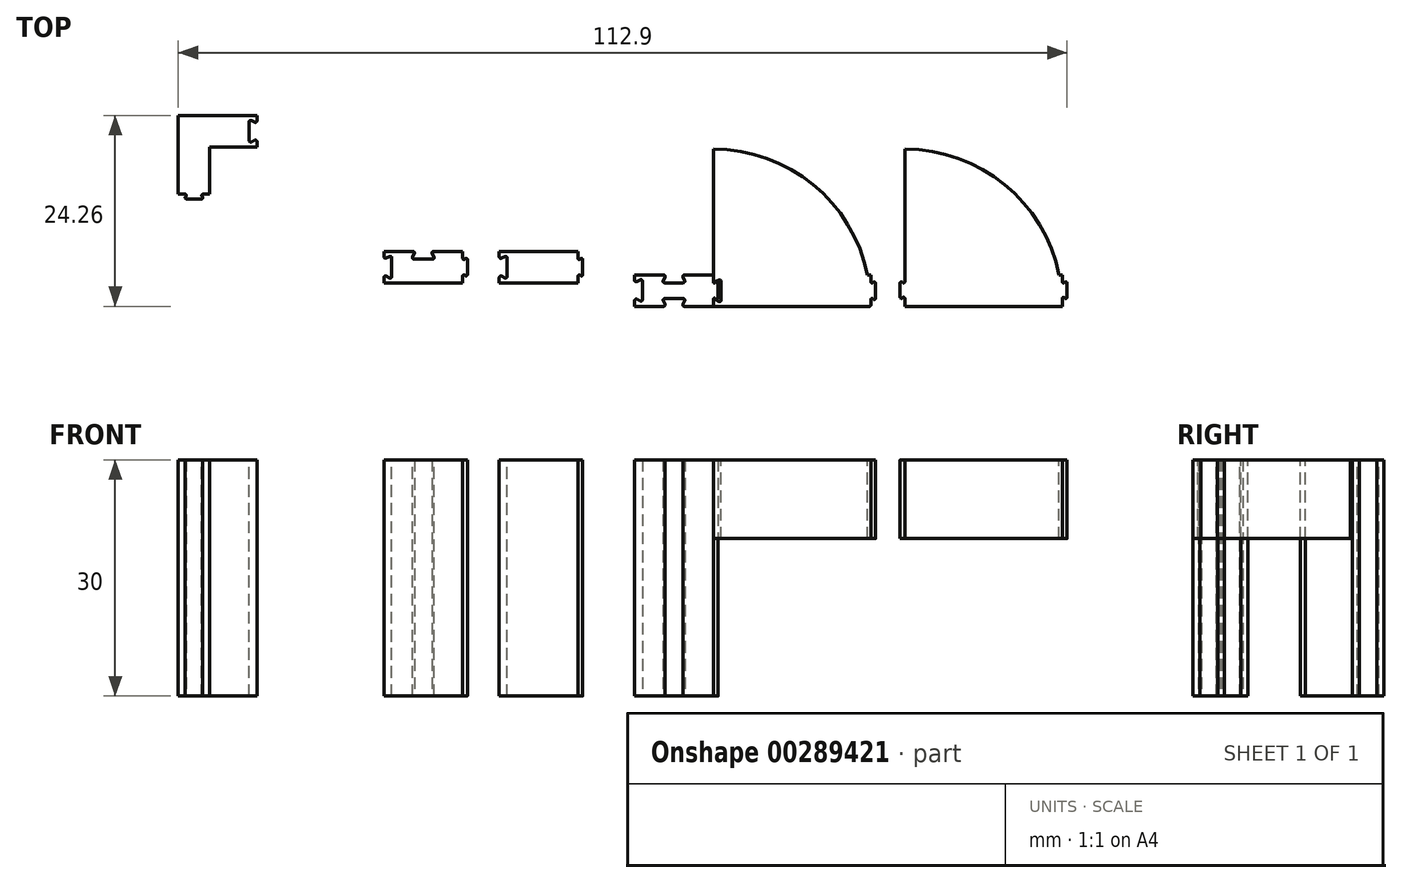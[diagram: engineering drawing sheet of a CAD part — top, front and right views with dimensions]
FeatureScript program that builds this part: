
annotation { "Feature Type Name" : "Feature", "Feature Type Description" : "" }
export const myFeature = defineFeature(function(context is Context, id is Id, definition is map)
    precondition{}
    {
        {
            var Q0;
            Q0=qCreatedBy(makeId("Top.planeOp"),FACE);
            var sketch = newSketch(context, id + "F0", { "sketchPlane" : qUnion([Q0])});
            skLineSegment(sketch, "E0.bottom", {"start": v(5, -2) * mm, "end": v(1.32, -2) * mm});
            skLineSegment(sketch, "E0.top", {"start": v(5, 2) * mm, "end": v(1.32, 2) * mm});
            skLineSegment(sketch, "E0.left", {"start": v(5, -2) * mm, "end": v(5, -1.1) * mm});
            skLineSegment(sketch, "E0.right", {"start": v(-5, -2) * mm, "end": v(-5, -1.27) * mm});
            skPoint(sketch, "E0.middle", {"position": v(0, 0) * mm});
            skLineSegment(sketch, "E1", {"start": v(-5, 0.03) * mm, "end": v(-4, 0.03) * mm});
            skPoint(sketch, "E1.endSnap0", {"position": v(-5, 0.03) * mm});
            skLineSegment(sketch, "E2", {"start": v(-4, 1.2) * mm, "end": v(-4, -1.13) * mm});
            skLineSegment(sketch, "E3", {"start": v(-4.7, 1.16) * mm, "end": v(-4.3, 1.38) * mm});
            skLineSegment(sketch, "E4", {"start": v(-4.7, -1.09) * mm, "end": v(-4.3, -1.3) * mm});
            skLineSegment(sketch, "E5", {"start": v(0, 2) * mm, "end": v(0, 1) * mm});
            skPoint(sketch, "E5.endSnap0", {"position": v(0, 2) * mm});
            skLineSegment(sketch, "E6", {"start": v(1.18, 1) * mm, "end": v(-1.18, 1) * mm});
            skLineSegment(sketch, "E7", {"start": v(-1.14, 1.71) * mm, "end": v(-1.36, 1.29) * mm});
            skLineSegment(sketch, "E8", {"start": v(1.14, 1.71) * mm, "end": v(1.36, 1.29) * mm});
            skLineSegment(sketch, "E9", {"start": v(5, 0) * mm, "end": v(5.6, 0) * mm});
            skPoint(sketch, "E9.endSnap0", {"position": v(5, 0) * mm});
            skLineSegment(sketch, "E10", {"start": v(5.6, 1) * mm, "end": v(5.6, -1) * mm});
            skLineSegment(sketch, "E11", {"start": v(5.23, 1) * mm, "end": v(5.37, 1.1) * mm});
            skLineSegment(sketch, "E12", {"start": v(5.37, -1.1) * mm, "end": v(5.23, -1) * mm});
            skLineSegment(sketch, "E13.MirrorCS", {"start": v(-1.14, -1.71) * mm, "end": v(-1.36, -1.29) * mm});
            skLineSegment(sketch, "E14.MirrorCS", {"start": v(1.14, -1.71) * mm, "end": v(1.36, -1.29) * mm});
            skLineSegment(sketch, "E15.MirrorCS", {"start": v(1.18, -1) * mm, "end": v(-1.18, -1) * mm});
            skLineSegment(sketch, "E16.trimOffspring", {"start": v(-1.32, 2) * mm, "end": v(-5, 2) * mm});
            skLineSegment(sketch, "E17.trimOffspring", {"start": v(5, 1.1) * mm, "end": v(5, 2) * mm});
            skLineSegment(sketch, "E18.trimOffspring", {"start": v(-1.32, -2) * mm, "end": v(-5, -2) * mm});
            skLineSegment(sketch, "E19.trimOffspring", {"start": v(-5, 1.33) * mm, "end": v(-5, 2) * mm});
            skPoint(sketch, "E20.visualSharp", {"position": v(-4, 1.53) * mm});
            skArc(sketch, "E20.filletArc", {"start": v(-4, 1.2) * mm, "mid": v(-4.1, 1.37) * mm, "end": v(-4.3, 1.38) * mm});
            skPoint(sketch, "E21.visualSharp", {"position": v(-4, -1.47) * mm});
            skArc(sketch, "E21.filletArc", {"start": v(-4.3, -1.3) * mm, "mid": v(-4.1, -1.3) * mm, "end": v(-4, -1.13) * mm});
            skPoint(sketch, "E22.visualSharp", {"position": v(-5, 1) * mm});
            skArc(sketch, "E22.filletArc", {"start": v(-5, 1.33) * mm, "mid": v(-4.9, 1.16) * mm, "end": v(-4.7, 1.16) * mm});
            skPoint(sketch, "E23.visualSharp", {"position": v(-5, -0.93) * mm});
            skArc(sketch, "E23.filletArc", {"start": v(-4.7, -1.09) * mm, "mid": v(-4.9, -1.1) * mm, "end": v(-5, -1.27) * mm});
            skPoint(sketch, "E24.visualSharp", {"position": v(-1, 2) * mm});
            skArc(sketch, "E24.filletArc", {"start": v(-1.14, 1.71) * mm, "mid": v(-1.15, 1.9) * mm, "end": v(-1.32, 2) * mm});
            skPoint(sketch, "E25.visualSharp", {"position": v(1, 2) * mm});
            skArc(sketch, "E25.filletArc", {"start": v(1.32, 2) * mm, "mid": v(1.15, 1.9) * mm, "end": v(1.14, 1.71) * mm});
            skPoint(sketch, "E26.visualSharp", {"position": v(1.5, 1) * mm});
            skArc(sketch, "E26.filletArc", {"start": v(1.18, 1) * mm, "mid": v(1.35, 1.1) * mm, "end": v(1.36, 1.29) * mm});
            skPoint(sketch, "E27.visualSharp", {"position": v(-1.5, 1) * mm});
            skArc(sketch, "E27.filletArc", {"start": v(-1.36, 1.29) * mm, "mid": v(-1.35, 1.1) * mm, "end": v(-1.18, 1) * mm});
            skPoint(sketch, "E28.visualSharp", {"position": v(-1.5, -1) * mm});
            skArc(sketch, "E28.filletArc", {"start": v(-1.18, -1) * mm, "mid": v(-1.35, -1.1) * mm, "end": v(-1.36, -1.29) * mm});
            skPoint(sketch, "E29.visualSharp", {"position": v(1.5, -1) * mm});
            skArc(sketch, "E29.filletArc", {"start": v(1.36, -1.29) * mm, "mid": v(1.35, -1.1) * mm, "end": v(1.18, -1) * mm});
            skPoint(sketch, "E30.visualSharp", {"position": v(1, -2) * mm});
            skArc(sketch, "E30.filletArc", {"start": v(1.14, -1.71) * mm, "mid": v(1.15, -1.9) * mm, "end": v(1.32, -2) * mm});
            skPoint(sketch, "E31.visualSharp", {"position": v(-1, -2) * mm});
            skArc(sketch, "E31.filletArc", {"start": v(-1.32, -2) * mm, "mid": v(-1.15, -1.9) * mm, "end": v(-1.14, -1.71) * mm});
            skPoint(sketch, "E32.visualSharp", {"position": v(5.6, 1.3) * mm});
            skArc(sketch, "E32.filletArc", {"start": v(5.6, 1) * mm, "mid": v(5.52, 1.13) * mm, "end": v(5.37, 1.1) * mm});
            skPoint(sketch, "E33.visualSharp", {"position": v(5.6, -1.3) * mm});
            skArc(sketch, "E33.filletArc", {"start": v(5.37, -1.1) * mm, "mid": v(5.52, -1.13) * mm, "end": v(5.6, -1) * mm});
            skPoint(sketch, "E34.visualSharp", {"position": v(5, -0.8) * mm});
            skArc(sketch, "E34.filletArc", {"start": v(5.23, -1) * mm, "mid": v(5.08, -0.97) * mm, "end": v(5, -1.1) * mm});
            skPoint(sketch, "E35.visualSharp", {"position": v(5, 0.8) * mm});
            skArc(sketch, "E35.filletArc", {"start": v(5, 1.1) * mm, "mid": v(5.08, 0.97) * mm, "end": v(5.23, 1) * mm});
            skSolve(sketch);
        }
        {
            var Q0;
            Q0=makeQuery(id+"F0.imprint","IMPRINT",FACE,{"disambiguationData":[TD([[makeQuery(id+"F0.imprint","IMPRINT",EDGE,{"derivedFrom":sQuery(id+"F0.wireOp",EDGE,"E0.bottom")}),-1.0]])]});
            extrude(context, id + "F1", {"entities" : qUnion([Q0]), "depth" : 30 * mm});
        }
        {
            var Q0;
            Q0=makeQuery(id+"F1.opExtrude","CAP_FACE",FACE,{"disambiguationData":[OSD([sQuery(id+"F0.wireOp",EDGE,"E0.bottom"),sQuery(id+"F0.wireOp",EDGE,"E0.top"),sQuery(id+"F0.wireOp",EDGE,"E0.left"),sQuery(id+"F0.wireOp",EDGE,"E0.right"),sQuery(id+"F0.wireOp",EDGE,"E2"),sQuery(id+"F0.wireOp",EDGE,"E3"),sQuery(id+"F0.wireOp",EDGE,"E4"),sQuery(id+"F0.wireOp",EDGE,"E6"),sQuery(id+"F0.wireOp",EDGE,"E7"),sQuery(id+"F0.wireOp",EDGE,"E8"),sQuery(id+"F0.wireOp",EDGE,"E10"),sQuery(id+"F0.wireOp",EDGE,"E11"),sQuery(id+"F0.wireOp",EDGE,"E12"),sQuery(id+"F0.wireOp",EDGE,"E13.MirrorCS"),sQuery(id+"F0.wireOp",EDGE,"E14.MirrorCS"),sQuery(id+"F0.wireOp",EDGE,"E15.MirrorCS"),sQuery(id+"F0.wireOp",EDGE,"E16.trimOffspring"),sQuery(id+"F0.wireOp",EDGE,"E17.trimOffspring"),sQuery(id+"F0.wireOp",EDGE,"E18.trimOffspring"),sQuery(id+"F0.wireOp",EDGE,"E19.trimOffspring"),sQuery(id+"F0.wireOp",EDGE,"E20.filletArc"),sQuery(id+"F0.wireOp",EDGE,"E21.filletArc"),sQuery(id+"F0.wireOp",EDGE,"E22.filletArc"),sQuery(id+"F0.wireOp",EDGE,"E23.filletArc"),sQuery(id+"F0.wireOp",EDGE,"E24.filletArc"),sQuery(id+"F0.wireOp",EDGE,"E25.filletArc"),sQuery(id+"F0.wireOp",EDGE,"E26.filletArc"),sQuery(id+"F0.wireOp",EDGE,"E27.filletArc"),sQuery(id+"F0.wireOp",EDGE,"E28.filletArc"),sQuery(id+"F0.wireOp",EDGE,"E29.filletArc"),sQuery(id+"F0.wireOp",EDGE,"E30.filletArc"),sQuery(id+"F0.wireOp",EDGE,"E31.filletArc"),sQuery(id+"F0.wireOp",EDGE,"E32.filletArc"),sQuery(id+"F0.wireOp",EDGE,"E33.filletArc"),sQuery(id+"F0.wireOp",EDGE,"E34.filletArc"),sQuery(id+"F0.wireOp",EDGE,"E35.filletArc")])],"isStart":false});
            var sketch = newSketch(context, id + "F2", { "sketchPlane" : qUnion([Q0])});
            skLineSegment(sketch, "E36", {"start": v(5, -2) * mm, "end": v(5, -1) * mm});
            skLineSegment(sketch, "E37", {"start": v(5, -2) * mm, "end": v(25, -2) * mm});
            skArc(sketch, "E38", {"start": v(24.6, 2) * mm, "mid": v(17.65, 13.5) * mm, "end": v(5, 18) * mm});
            skLineSegment(sketch, "E39", {"start": v(5, 0) * mm, "end": v(6, 0) * mm});
            skPoint(sketch, "E39.endSnap0", {"position": v(5, 0) * mm});
            skLineSegment(sketch, "E40", {"start": v(6, 1.5) * mm, "end": v(6, -1.5) * mm});
            skLineSegment(sketch, "E41", {"start": v(5, 1) * mm, "end": v(6, 1.5) * mm});
            skLineSegment(sketch, "E42", {"start": v(5, -1) * mm, "end": v(6, -1.5) * mm});
            skLineSegment(sketch, "E43.trimOffspring", {"start": v(5, 1) * mm, "end": v(5, 18) * mm});
            skLineSegment(sketch, "E44", {"start": v(24.6, 2) * mm, "end": v(25, 2) * mm});
            skLineSegment(sketch, "E45", {"start": v(25, 2) * mm, "end": v(25, 0.8) * mm});
            skLineSegment(sketch, "E46", {"start": v(25, 0) * mm, "end": v(25.6, 0) * mm});
            skPoint(sketch, "E46.endSnap0", {"position": v(25, 0) * mm});
            skLineSegment(sketch, "E47", {"start": v(25.6, 1.3) * mm, "end": v(25.6, -1.3) * mm});
            skLineSegment(sketch, "E48", {"start": v(25, 0.8) * mm, "end": v(25.6, 1.3) * mm});
            skLineSegment(sketch, "E49", {"start": v(25, -0.8) * mm, "end": v(25.6, -1.3) * mm});
            skLineSegment(sketch, "E50.trimOffspring", {"start": v(25, -0.8) * mm, "end": v(25, -2) * mm});
            skSolve(sketch);
        }
        {
            var Q0;
            {var subQ17=sQuery(id+"F2.wireOp",EDGE,"E37");Q0=makeQuery(id+"F2.imprint","IMPRINT",FACE,{"disambiguationData":[TD([[makeQuery(id+"F2.imprint","IMPRINT",EDGE,{"derivedFrom":subQ17}),1.0]])]});}
            extrude(context, id + "F3", {"entities" : qUnion([Q0]), "oppositeDirection" : true, "depth" : 10 * mm});
        }
        {
            var Q0;
            Q0=makeQuery(id+"F3.opExtrude","SWEPT_EDGE",EDGE,{"disambiguationData":[OSD([sQuery(id+"F0.wireOp",EDGE,"E35.filletArc"),sQuery(id+"F2.wireOp",EDGE,"E41")])]});
            var Q1;
            Q1=makeQuery(id+"F3.opExtrude","SWEPT_EDGE",EDGE,{"disambiguationData":[OSD([sQuery(id+"F2.wireOp",EDGE,"E40"),sQuery(id+"F2.wireOp",EDGE,"E41")])]});
            var Q2;
            Q2=makeQuery(id+"F3.opExtrude","SWEPT_EDGE",EDGE,{"disambiguationData":[OSD([sQuery(id+"F2.wireOp",EDGE,"E40"),sQuery(id+"F2.wireOp",EDGE,"E42")])]});
            var Q3;
            Q3=makeQuery(id+"F3.opExtrude","SWEPT_EDGE",EDGE,{"disambiguationData":[OSD([sQuery(id+"F0.wireOp",EDGE,"E34.filletArc"),sQuery(id+"F2.wireOp",EDGE,"E42")])]});
            fillet(context, id + "F4", {"entities" : qUnion([Q0, Q1, Q2, Q3]), "radius" : 0.2 * mm, "tangentPropagation" : true, "allowEdgeOverflow" : false});
        }
        {
            var Q0;
            Q0=makeQuery(id+"F3.opExtrude","SWEPT_EDGE",EDGE,{"disambiguationData":[OSD([sQuery(id+"F2.wireOp",EDGE,"kMCYHtvS-aAIt-fest-USlL-1YW07ew3pKTC"),sQuery(id+"F2.wireOp",EDGE,"vUYih6yE-jNni-61bJ-aQ8p-8MaSVhB4adIa")])]});
            var Q1;
            Q1=makeQuery(id+"F3.opExtrude","SWEPT_EDGE",EDGE,{"disambiguationData":[OSD([sQuery(id+"F2.wireOp",EDGE,"wb0FoicF-ZCbF-01Gs-8v7q-hL0EyNRj5M07"),sQuery(id+"F2.wireOp",EDGE,"vUYih6yE-jNni-61bJ-aQ8p-8MaSVhB4adIa")])]});
            var Q2;
            Q2=makeQuery(id+"F3.opExtrude","SWEPT_EDGE",EDGE,{"disambiguationData":[OSD([sQuery(id+"F2.wireOp",EDGE,"wb0FoicF-ZCbF-01Gs-8v7q-hL0EyNRj5M07"),sQuery(id+"F2.wireOp",EDGE,"AaNN7OY1-jFjU-YAYL-W6Cu-X6FdF49Wq9E5")])]});
            var Q3;
            Q3=makeQuery(id+"F3.opExtrude","SWEPT_EDGE",EDGE,{"disambiguationData":[OSD([sQuery(id+"F2.wireOp",EDGE,"f3f7dbc3-d528-4954-9ca2-8d0361898fbf.trimOffspring"),sQuery(id+"F2.wireOp",EDGE,"AaNN7OY1-jFjU-YAYL-W6Cu-X6FdF49Wq9E5")])]});
            var Q4;
            Q4=makeQuery(id+"F3.opExtrude","SWEPT_EDGE",EDGE,{"disambiguationData":[OSD([sQuery(id+"F2.wireOp",EDGE,"E37"),sQuery(id+"F2.wireOp",EDGE,"f3f7dbc3-d528-4954-9ca2-8d0361898fbf.trimOffspring")])]});
            fillet(context, id + "F5", {"entities" : qUnion([Q0, Q1, Q2, Q3, Q4]), "radius" : 0.16 * mm, "tangentPropagation" : true, "allowEdgeOverflow" : false});
        }
        {
            var Q0;
            Q0=makeQuery(id+"F3.opExtrude","CAP_FACE",FACE,{"disambiguationData":[OSD([sQuery(id+"F0.wireOp",EDGE,"E34.filletArc"),sQuery(id+"F0.wireOp",EDGE,"E35.filletArc"),sQuery(id+"F2.wireOp",EDGE,"E36"),sQuery(id+"F2.wireOp",EDGE,"E37"),sQuery(id+"F2.wireOp",EDGE,"E38"),sQuery(id+"F2.wireOp",EDGE,"kMCYHtvS-aAIt-fest-USlL-1YW07ew3pKTC"),sQuery(id+"F2.wireOp",EDGE,"f3f7dbc3-d528-4954-9ca2-8d0361898fbf.trimOffspring"),sQuery(id+"F2.wireOp",EDGE,"wb0FoicF-ZCbF-01Gs-8v7q-hL0EyNRj5M07"),sQuery(id+"F2.wireOp",EDGE,"vUYih6yE-jNni-61bJ-aQ8p-8MaSVhB4adIa"),sQuery(id+"F2.wireOp",EDGE,"AaNN7OY1-jFjU-YAYL-W6Cu-X6FdF49Wq9E5"),sQuery(id+"F2.wireOp",EDGE,"E40"),sQuery(id+"F2.wireOp",EDGE,"E41"),sQuery(id+"F2.wireOp",EDGE,"E42"),sQuery(id+"F2.wireOp",EDGE,"E43.trimOffspring"),sQuery(id+"F2.wireOp",EDGE,"E44")])],"isStart":true});
            var sketch = newSketch(context, id + "F6", { "sketchPlane" : qUnion([Q0])});
            skLineSegment(sketch, "E51", {"start": v(29.33, -2) * mm, "end": v(29.33, -0.54) * mm});
            skLineSegment(sketch, "E52", {"start": v(29.33, -2) * mm, "end": v(49.33, -2) * mm});
            skArc(sketch, "E53", {"start": v(48.93, 2) * mm, "mid": v(41.98, 13.5) * mm, "end": v(29.33, 18) * mm});
            skLineSegment(sketch, "E54", {"start": v(24.6, 2) * mm, "end": v(53.57, 2) * mm, "construction": true});
            skLineSegment(sketch, "E55", {"start": v(49.33, -2) * mm, "end": v(49.33, -0.54) * mm});
            skLineSegment(sketch, "E56", {"start": v(49.33, 2) * mm, "end": v(48.93, 2) * mm});
            skPoint(sketch, "E57", {"position": v(49.33, 0) * mm});
            skLineSegment(sketch, "E58", {"start": v(49.33, 0) * mm, "end": v(49.93, 0) * mm});
            skLineSegment(sketch, "E59", {"start": v(49.93, 1.3) * mm, "end": v(49.93, -1.3) * mm});
            skLineSegment(sketch, "E60", {"start": v(49.33, 0.8) * mm, "end": v(49.93, 1.3) * mm});
            skLineSegment(sketch, "E61", {"start": v(49.93, -1.3) * mm, "end": v(49.33, -0.54) * mm});
            skLineSegment(sketch, "E62.trimOffspring", {"start": v(49.33, 0.8) * mm, "end": v(49.33, 2) * mm});
            skPoint(sketch, "E63", {"position": v(39.33, -2) * mm});
            skLineSegment(sketch, "E64", {"start": v(39.33, -2.86) * mm, "end": v(39.33, 12.14) * mm});
            skLineSegment(sketch, "E65.MirrorCS", {"start": v(29.33, 0.8) * mm, "end": v(28.73, 1.3) * mm});
            skLineSegment(sketch, "E66.MirrorCS", {"start": v(28.73, 1.3) * mm, "end": v(28.73, -1.3) * mm});
            skLineSegment(sketch, "E67.MirrorCS", {"start": v(28.73, -1.3) * mm, "end": v(29.33, -0.54) * mm});
            skLineSegment(sketch, "E68.trimOffspring", {"start": v(29.33, 0.8) * mm, "end": v(29.33, 18) * mm});
            skLineSegment(sketch, "E69.0", {"start": v(5, -2) * mm, "end": v(24.84, -2) * mm});
            skSolve(sketch);
        }
        {
            var Q0;
            {var subQ4=sQuery(id+"F6.wireOp",EDGE,"E51");Q0=makeQuery(id+"F6.imprint","IMPRINT",FACE,{"disambiguationData":[TD([[makeQuery(id+"F6.imprint","IMPRINT",EDGE,{"derivedFrom":subQ4}),-1.0]])]});}
            extrude(context, id + "F7", {"entities" : qUnion([Q0]), "oppositeDirection" : true, "depth" : 10 * mm});
        }
        {
            var Q0;
            Q0=makeQuery(id+"F7.opExtrude","SWEPT_EDGE",EDGE,{"disambiguationData":[OSD([sQuery(id+"F6.wireOp",EDGE,"E51"),sQuery(id+"F6.wireOp",EDGE,"E67.MirrorCS")])]});
            var Q1;
            Q1=makeQuery(id+"F7.opExtrude","SWEPT_EDGE",EDGE,{"disambiguationData":[OSD([sQuery(id+"F6.wireOp",EDGE,"E66.MirrorCS"),sQuery(id+"F6.wireOp",EDGE,"E67.MirrorCS")])]});
            var Q2;
            Q2=makeQuery(id+"F7.opExtrude","SWEPT_EDGE",EDGE,{"disambiguationData":[OSD([sQuery(id+"F6.wireOp",EDGE,"E65.MirrorCS"),sQuery(id+"F6.wireOp",EDGE,"E66.MirrorCS")])]});
            var Q3;
            Q3=makeQuery(id+"F7.opExtrude","SWEPT_EDGE",EDGE,{"disambiguationData":[OSD([sQuery(id+"F6.wireOp",EDGE,"E65.MirrorCS"),sQuery(id+"F6.wireOp",EDGE,"E68.trimOffspring")])]});
            var Q4;
            Q4=makeQuery(id+"F7.opExtrude","SWEPT_EDGE",EDGE,{"disambiguationData":[OSD([sQuery(id+"F6.wireOp",EDGE,"E60"),sQuery(id+"F6.wireOp",EDGE,"E62.trimOffspring")])]});
            var Q5;
            Q5=makeQuery(id+"F7.opExtrude","SWEPT_EDGE",EDGE,{"disambiguationData":[OSD([sQuery(id+"F6.wireOp",EDGE,"E59"),sQuery(id+"F6.wireOp",EDGE,"E60")])]});
            var Q6;
            Q6=makeQuery(id+"F7.opExtrude","SWEPT_EDGE",EDGE,{"disambiguationData":[OSD([sQuery(id+"F6.wireOp",EDGE,"E59"),sQuery(id+"F6.wireOp",EDGE,"E61")])]});
            var Q7;
            Q7=makeQuery(id+"F7.opExtrude","SWEPT_EDGE",EDGE,{"disambiguationData":[OSD([sQuery(id+"F6.wireOp",EDGE,"E55"),sQuery(id+"F6.wireOp",EDGE,"E61")])]});
            fillet(context, id + "F8", {"entities" : qUnion([Q0, Q1, Q2, Q3, Q4, Q5, Q6, Q7]), "radius" : 0.16 * mm, "tangentPropagation" : true, "allowEdgeOverflow" : false});
        }
        {
            var Q0;
            Q0=makeQuery(id+"F3.opExtrude","SWEPT_EDGE",EDGE,{"disambiguationData":[OSD([sQuery(id+"F2.wireOp",EDGE,"E45"),sQuery(id+"F2.wireOp",EDGE,"E48")])]});
            var Q1;
            Q1=makeQuery(id+"F3.opExtrude","SWEPT_EDGE",EDGE,{"disambiguationData":[OSD([sQuery(id+"F2.wireOp",EDGE,"E47"),sQuery(id+"F2.wireOp",EDGE,"E48")])]});
            var Q2;
            Q2=makeQuery(id+"F3.opExtrude","SWEPT_EDGE",EDGE,{"disambiguationData":[OSD([sQuery(id+"F2.wireOp",EDGE,"E49"),sQuery(id+"F2.wireOp",EDGE,"E50.trimOffspring")])]});
            var Q3;
            Q3=makeQuery(id+"F3.opExtrude","SWEPT_EDGE",EDGE,{"disambiguationData":[OSD([sQuery(id+"F2.wireOp",EDGE,"E47"),sQuery(id+"F2.wireOp",EDGE,"E49")])]});
            fillet(context, id + "F9", {"entities" : qUnion([Q0, Q1, Q2, Q3]), "radius" : 0.16 * mm, "tangentPropagation" : true, "allowEdgeOverflow" : false});
        }
        {
            var Q0;
            Q0=makeQuery(id+"F1.opExtrude","CAP_FACE",FACE,{"disambiguationData":[OSD([sQuery(id+"F0.wireOp",EDGE,"E0.bottom"),sQuery(id+"F0.wireOp",EDGE,"E0.top"),sQuery(id+"F0.wireOp",EDGE,"E0.left"),sQuery(id+"F0.wireOp",EDGE,"E0.right"),sQuery(id+"F0.wireOp",EDGE,"E2"),sQuery(id+"F0.wireOp",EDGE,"E3"),sQuery(id+"F0.wireOp",EDGE,"E4"),sQuery(id+"F0.wireOp",EDGE,"E6"),sQuery(id+"F0.wireOp",EDGE,"E7"),sQuery(id+"F0.wireOp",EDGE,"E8"),sQuery(id+"F0.wireOp",EDGE,"E10"),sQuery(id+"F0.wireOp",EDGE,"E11"),sQuery(id+"F0.wireOp",EDGE,"E12"),sQuery(id+"F0.wireOp",EDGE,"E13.MirrorCS"),sQuery(id+"F0.wireOp",EDGE,"E14.MirrorCS"),sQuery(id+"F0.wireOp",EDGE,"E15.MirrorCS"),sQuery(id+"F0.wireOp",EDGE,"E16.trimOffspring"),sQuery(id+"F0.wireOp",EDGE,"E17.trimOffspring"),sQuery(id+"F0.wireOp",EDGE,"E18.trimOffspring"),sQuery(id+"F0.wireOp",EDGE,"E19.trimOffspring"),sQuery(id+"F0.wireOp",EDGE,"E20.filletArc"),sQuery(id+"F0.wireOp",EDGE,"E21.filletArc"),sQuery(id+"F0.wireOp",EDGE,"E22.filletArc"),sQuery(id+"F0.wireOp",EDGE,"E23.filletArc"),sQuery(id+"F0.wireOp",EDGE,"E24.filletArc"),sQuery(id+"F0.wireOp",EDGE,"E25.filletArc"),sQuery(id+"F0.wireOp",EDGE,"E26.filletArc"),sQuery(id+"F0.wireOp",EDGE,"E27.filletArc"),sQuery(id+"F0.wireOp",EDGE,"E28.filletArc"),sQuery(id+"F0.wireOp",EDGE,"E29.filletArc"),sQuery(id+"F0.wireOp",EDGE,"E30.filletArc"),sQuery(id+"F0.wireOp",EDGE,"E31.filletArc"),sQuery(id+"F0.wireOp",EDGE,"E32.filletArc"),sQuery(id+"F0.wireOp",EDGE,"E33.filletArc"),sQuery(id+"F0.wireOp",EDGE,"E34.filletArc"),sQuery(id+"F0.wireOp",EDGE,"E35.filletArc")])],"isStart":false});
            var sketch = newSketch(context, id + "F10", { "sketchPlane" : qUnion([Q0])});
            skLineSegment(sketch, "E70.bottom", {"start": v(-62.97, 12.26) * mm, "end": v(-61.77, 12.26) * mm});
            skLineSegment(sketch, "E70.top", {"start": v(-62.97, 22.26) * mm, "end": v(-52.97, 22.26) * mm});
            skLineSegment(sketch, "E70.left", {"start": v(-62.97, 12.26) * mm, "end": v(-62.97, 22.26) * mm});
            skLineSegment(sketch, "E70.right", {"start": v(-52.97, 18.26) * mm, "end": v(-52.97, 19.26) * mm});
            skLineSegment(sketch, "E71.top", {"start": v(-52.97, 18.26) * mm, "end": v(-58.97, 18.26) * mm});
            skLineSegment(sketch, "E71.right", {"start": v(-58.97, 12.26) * mm, "end": v(-58.97, 18.26) * mm});
            skPoint(sketch, "E72", {"position": v(-60.97, 12.26) * mm});
            skLineSegment(sketch, "E73", {"start": v(-62.27, 11.66) * mm, "end": v(-59.67, 11.66) * mm});
            skLineSegment(sketch, "E74", {"start": v(-61.77, 12.26) * mm, "end": v(-62.27, 11.66) * mm});
            skLineSegment(sketch, "E75", {"start": v(-60.17, 12.26) * mm, "end": v(-59.67, 11.66) * mm});
            skPoint(sketch, "E76.end.orphan", {"position": v(-60.97, 11.66) * mm});
            skLineSegment(sketch, "E77.trimOffspring", {"start": v(-60.17, 12.26) * mm, "end": v(-58.97, 12.26) * mm});
            skPoint(sketch, "E78", {"position": v(-52.97, 20.26) * mm});
            skLineSegment(sketch, "E79", {"start": v(-53.97, 21.76) * mm, "end": v(-53.97, 18.76) * mm});
            skLineSegment(sketch, "E80", {"start": v(-53.97, 21.76) * mm, "end": v(-52.97, 21.26) * mm});
            skLineSegment(sketch, "E81", {"start": v(-52.97, 19.26) * mm, "end": v(-53.97, 18.76) * mm});
            skLineSegment(sketch, "E82.trimOffspring", {"start": v(-52.97, 21.26) * mm, "end": v(-52.97, 22.26) * mm});
            skPoint(sketch, "E83.end.orphan", {"position": v(-53.97, 20.26) * mm});
            skSolve(sketch);
        }
        {
            var Q0;
            Q0 = qSketchRegion(id + "F10", true);
            extrude(context, id + "F11", {"entities" : qUnion([Q0]), "oppositeDirection" : true, "depth" : 30 * mm});
        }
        {
            var Q0;
            Q0=makeQuery(id+"F11.opExtrude","SWEPT_EDGE",EDGE,{"disambiguationData":[OSD([sQuery(id+"F10.wireOp",EDGE,"E73"),sQuery(id+"F10.wireOp",EDGE,"E75")])]});
            var Q1;
            Q1=makeQuery(id+"F11.opExtrude","SWEPT_EDGE",EDGE,{"disambiguationData":[OSD([sQuery(id+"F10.wireOp",EDGE,"E73"),sQuery(id+"F10.wireOp",EDGE,"E74")])]});
            var Q2;
            Q2=makeQuery(id+"F11.opExtrude","SWEPT_EDGE",EDGE,{"disambiguationData":[OSD([sQuery(id+"F10.wireOp",EDGE,"E70.bottom"),sQuery(id+"F10.wireOp",EDGE,"E74")])]});
            var Q3;
            Q3=makeQuery(id+"F11.opExtrude","SWEPT_EDGE",EDGE,{"disambiguationData":[OSD([sQuery(id+"F10.wireOp",EDGE,"E75"),sQuery(id+"F10.wireOp",EDGE,"E77.trimOffspring")])]});
            fillet(context, id + "F12", {"entities" : qUnion([Q0, Q1, Q2, Q3]), "radius" : 0.16 * mm, "tangentPropagation" : true, "allowEdgeOverflow" : false});
        }
        {
            var Q0;
            Q0=makeQuery(id+"F11.opExtrude","SWEPT_EDGE",EDGE,{"disambiguationData":[OSD([sQuery(id+"F10.wireOp",EDGE,"E80"),sQuery(id+"F10.wireOp",EDGE,"E82.trimOffspring")])]});
            var Q1;
            Q1=makeQuery(id+"F11.opExtrude","SWEPT_EDGE",EDGE,{"disambiguationData":[OSD([sQuery(id+"F10.wireOp",EDGE,"E79"),sQuery(id+"F10.wireOp",EDGE,"E80")])]});
            var Q2;
            Q2=makeQuery(id+"F11.opExtrude","SWEPT_EDGE",EDGE,{"disambiguationData":[OSD([sQuery(id+"F10.wireOp",EDGE,"E70.right"),sQuery(id+"F10.wireOp",EDGE,"E81")])]});
            var Q3;
            Q3=makeQuery(id+"F11.opExtrude","SWEPT_EDGE",EDGE,{"disambiguationData":[OSD([sQuery(id+"F10.wireOp",EDGE,"E79"),sQuery(id+"F10.wireOp",EDGE,"E81")])]});
            fillet(context, id + "F13", {"entities" : qUnion([Q0, Q1, Q2, Q3]), "radius" : 0.2 * mm, "tangentPropagation" : true, "allowEdgeOverflow" : false});
        }
        {
            var Q0;
            Q0=makeQuery(id+"F1.opExtrude","CAP_FACE",FACE,{"disambiguationData":[OSD([sQuery(id+"F0.wireOp",EDGE,"E0.bottom"),sQuery(id+"F0.wireOp",EDGE,"E0.top"),sQuery(id+"F0.wireOp",EDGE,"E0.left"),sQuery(id+"F0.wireOp",EDGE,"E0.right"),sQuery(id+"F0.wireOp",EDGE,"E2"),sQuery(id+"F0.wireOp",EDGE,"E3"),sQuery(id+"F0.wireOp",EDGE,"E4"),sQuery(id+"F0.wireOp",EDGE,"E6"),sQuery(id+"F0.wireOp",EDGE,"E7"),sQuery(id+"F0.wireOp",EDGE,"E8"),sQuery(id+"F0.wireOp",EDGE,"E10"),sQuery(id+"F0.wireOp",EDGE,"E11"),sQuery(id+"F0.wireOp",EDGE,"E12"),sQuery(id+"F0.wireOp",EDGE,"E13.MirrorCS"),sQuery(id+"F0.wireOp",EDGE,"E14.MirrorCS"),sQuery(id+"F0.wireOp",EDGE,"E15.MirrorCS"),sQuery(id+"F0.wireOp",EDGE,"E16.trimOffspring"),sQuery(id+"F0.wireOp",EDGE,"E17.trimOffspring"),sQuery(id+"F0.wireOp",EDGE,"E18.trimOffspring"),sQuery(id+"F0.wireOp",EDGE,"E19.trimOffspring"),sQuery(id+"F0.wireOp",EDGE,"E20.filletArc"),sQuery(id+"F0.wireOp",EDGE,"E21.filletArc"),sQuery(id+"F0.wireOp",EDGE,"E22.filletArc"),sQuery(id+"F0.wireOp",EDGE,"E23.filletArc"),sQuery(id+"F0.wireOp",EDGE,"E24.filletArc"),sQuery(id+"F0.wireOp",EDGE,"E25.filletArc"),sQuery(id+"F0.wireOp",EDGE,"E26.filletArc"),sQuery(id+"F0.wireOp",EDGE,"E27.filletArc"),sQuery(id+"F0.wireOp",EDGE,"E28.filletArc"),sQuery(id+"F0.wireOp",EDGE,"E29.filletArc"),sQuery(id+"F0.wireOp",EDGE,"E30.filletArc"),sQuery(id+"F0.wireOp",EDGE,"E31.filletArc"),sQuery(id+"F0.wireOp",EDGE,"E32.filletArc"),sQuery(id+"F0.wireOp",EDGE,"E33.filletArc"),sQuery(id+"F0.wireOp",EDGE,"E34.filletArc"),sQuery(id+"F0.wireOp",EDGE,"E35.filletArc")])],"isStart":false});
            var sketch = newSketch(context, id + "F14", { "sketchPlane" : qUnion([Q0])});
            skLineSegment(sketch, "E84.bottom", {"start": v(-36.84, 4.99) * mm, "end": v(-32.84, 4.99) * mm});
            skLineSegment(sketch, "E84.top", {"start": v(-36.84, 0.99) * mm, "end": v(-26.84, 0.99) * mm});
            skLineSegment(sketch, "E84.left", {"start": v(-36.84, 4.99) * mm, "end": v(-36.84, 3.99) * mm});
            skLineSegment(sketch, "E84.right", {"start": v(-26.84, 4.99) * mm, "end": v(-26.84, 3.79) * mm});
            skPoint(sketch, "E85", {"position": v(-36.84, 2.99) * mm});
            skPoint(sketch, "E86", {"position": v(-31.84, 4.99) * mm});
            skLineSegment(sketch, "E87", {"start": v(-35.84, 4.49) * mm, "end": v(-35.84, 1.49) * mm});
            skLineSegment(sketch, "E88", {"start": v(-36.84, 3.99) * mm, "end": v(-35.84, 4.49) * mm});
            skLineSegment(sketch, "E89", {"start": v(-36.84, 1.99) * mm, "end": v(-35.84, 1.49) * mm});
            skLineSegment(sketch, "E90", {"start": v(-33.34, 3.99) * mm, "end": v(-30.34, 3.99) * mm});
            skLineSegment(sketch, "E91", {"start": v(-33.34, 3.99) * mm, "end": v(-32.84, 4.99) * mm});
            skLineSegment(sketch, "E92", {"start": v(-30.84, 4.99) * mm, "end": v(-30.34, 3.99) * mm});
            skPoint(sketch, "E93", {"position": v(-26.84, 2.99) * mm});
            skLineSegment(sketch, "E94", {"start": v(-26.24, 4.29) * mm, "end": v(-26.24, 1.69) * mm});
            skLineSegment(sketch, "E95", {"start": v(-26.84, 3.79) * mm, "end": v(-26.24, 4.29) * mm});
            skLineSegment(sketch, "E96", {"start": v(-26.84, 2.19) * mm, "end": v(-26.24, 1.69) * mm});
            skPoint(sketch, "E97.end.orphan", {"position": v(-35.84, 2.99) * mm});
            skLineSegment(sketch, "E98.trimOffspring", {"start": v(-36.84, 1.99) * mm, "end": v(-36.84, 0.99) * mm});
            skLineSegment(sketch, "E99.trimOffspring", {"start": v(-30.84, 4.99) * mm, "end": v(-26.84, 4.99) * mm});
            skPoint(sketch, "E100.end.orphan", {"position": v(-31.84, 3.99) * mm});
            skPoint(sketch, "E101.end.orphan", {"position": v(-26.24, 2.99) * mm});
            skLineSegment(sketch, "E102.trimOffspring", {"start": v(-26.84, 2.19) * mm, "end": v(-26.84, 0.99) * mm});
            skSolve(sketch);
        }
        {
            var Q0;
            Q0 = qSketchRegion(id + "F14", true);
            extrude(context, id + "F15", {"entities" : qUnion([Q0]), "oppositeDirection" : true, "depth" : 30 * mm});
        }
        {
            var Q0;
            Q0=makeQuery(id+"F15.opExtrude","SWEPT_EDGE",EDGE,{"disambiguationData":[OSD([sQuery(id+"F14.wireOp",EDGE,"E84.left"),sQuery(id+"F14.wireOp",EDGE,"E88")])]});
            var Q1;
            Q1=makeQuery(id+"F15.opExtrude","SWEPT_EDGE",EDGE,{"disambiguationData":[OSD([sQuery(id+"F14.wireOp",EDGE,"E87"),sQuery(id+"F14.wireOp",EDGE,"E88")])]});
            var Q2;
            Q2=makeQuery(id+"F15.opExtrude","SWEPT_EDGE",EDGE,{"disambiguationData":[OSD([sQuery(id+"F14.wireOp",EDGE,"E87"),sQuery(id+"F14.wireOp",EDGE,"E89")])]});
            var Q3;
            Q3=makeQuery(id+"F15.opExtrude","SWEPT_EDGE",EDGE,{"disambiguationData":[OSD([sQuery(id+"F14.wireOp",EDGE,"E89"),sQuery(id+"F14.wireOp",EDGE,"E98.trimOffspring")])]});
            var Q4;
            Q4=makeQuery(id+"F15.opExtrude","SWEPT_EDGE",EDGE,{"disambiguationData":[OSD([sQuery(id+"F14.wireOp",EDGE,"E84.bottom"),sQuery(id+"F14.wireOp",EDGE,"E91")])]});
            var Q5;
            Q5=makeQuery(id+"F15.opExtrude","SWEPT_EDGE",EDGE,{"disambiguationData":[OSD([sQuery(id+"F14.wireOp",EDGE,"E92"),sQuery(id+"F14.wireOp",EDGE,"E99.trimOffspring")])]});
            var Q6;
            Q6=makeQuery(id+"F15.opExtrude","SWEPT_EDGE",EDGE,{"disambiguationData":[OSD([sQuery(id+"F14.wireOp",EDGE,"E90"),sQuery(id+"F14.wireOp",EDGE,"E92")])]});
            var Q7;
            Q7=makeQuery(id+"F15.opExtrude","SWEPT_EDGE",EDGE,{"disambiguationData":[OSD([sQuery(id+"F14.wireOp",EDGE,"E90"),sQuery(id+"F14.wireOp",EDGE,"E91")])]});
            fillet(context, id + "F16", {"entities" : qUnion([Q0, Q1, Q2, Q3, Q4, Q5, Q6, Q7]), "radius" : 0.2 * mm, "tangentPropagation" : true, "allowEdgeOverflow" : false});
        }
        {
            var Q0;
            Q0=makeQuery(id+"F15.opExtrude","SWEPT_EDGE",EDGE,{"disambiguationData":[OSD([sQuery(id+"F14.wireOp",EDGE,"E94"),sQuery(id+"F14.wireOp",EDGE,"E95")])]});
            var Q1;
            Q1=makeQuery(id+"F15.opExtrude","SWEPT_EDGE",EDGE,{"disambiguationData":[OSD([sQuery(id+"F14.wireOp",EDGE,"E94"),sQuery(id+"F14.wireOp",EDGE,"E96")])]});
            var Q2;
            Q2=makeQuery(id+"F15.opExtrude","SWEPT_EDGE",EDGE,{"disambiguationData":[OSD([sQuery(id+"F14.wireOp",EDGE,"E84.right"),sQuery(id+"F14.wireOp",EDGE,"E95")])]});
            var Q3;
            Q3=makeQuery(id+"F15.opExtrude","SWEPT_EDGE",EDGE,{"disambiguationData":[OSD([sQuery(id+"F14.wireOp",EDGE,"E96"),sQuery(id+"F14.wireOp",EDGE,"E102.trimOffspring")])]});
            fillet(context, id + "F17", {"entities" : qUnion([Q0, Q1, Q2, Q3]), "radius" : 0.16 * mm, "tangentPropagation" : true, "allowEdgeOverflow" : false});
        }
        {
            var Q0;
            Q0=makeQuery(id+"F15.opExtrude","CAP_FACE",FACE,{"disambiguationData":[OSD([sQuery(id+"F14.wireOp",EDGE,"E84.bottom"),sQuery(id+"F14.wireOp",EDGE,"E84.top"),sQuery(id+"F14.wireOp",EDGE,"E84.left"),sQuery(id+"F14.wireOp",EDGE,"E84.right"),sQuery(id+"F14.wireOp",EDGE,"E87"),sQuery(id+"F14.wireOp",EDGE,"E88"),sQuery(id+"F14.wireOp",EDGE,"E89"),sQuery(id+"F14.wireOp",EDGE,"E90"),sQuery(id+"F14.wireOp",EDGE,"E91"),sQuery(id+"F14.wireOp",EDGE,"E92"),sQuery(id+"F14.wireOp",EDGE,"E94"),sQuery(id+"F14.wireOp",EDGE,"E95"),sQuery(id+"F14.wireOp",EDGE,"E96"),sQuery(id+"F14.wireOp",EDGE,"E98.trimOffspring"),sQuery(id+"F14.wireOp",EDGE,"E99.trimOffspring"),sQuery(id+"F14.wireOp",EDGE,"E102.trimOffspring")])],"isStart":true});
            var sketch = newSketch(context, id + "F18", { "sketchPlane" : qUnion([Q0])});
            skLineSegment(sketch, "E103.bottom", {"start": v(-22.19, 0.99) * mm, "end": v(-12.19, 0.99) * mm});
            skLineSegment(sketch, "E103.top", {"start": v(-22.19, 4.99) * mm, "end": v(-12.19, 4.99) * mm});
            skLineSegment(sketch, "E103.left", {"start": v(-22.19, 0.99) * mm, "end": v(-22.19, 1.99) * mm});
            skLineSegment(sketch, "E103.right", {"start": v(-12.19, 0.99) * mm, "end": v(-12.19, 2.19) * mm});
            skPoint(sketch, "E104", {"position": v(-22.19, 2.99) * mm});
            skLineSegment(sketch, "E105", {"start": v(-21.19, 4.49) * mm, "end": v(-21.19, 1.49) * mm});
            skLineSegment(sketch, "E106", {"start": v(-22.19, 3.99) * mm, "end": v(-21.19, 4.49) * mm});
            skLineSegment(sketch, "E107", {"start": v(-21.19, 1.49) * mm, "end": v(-22.19, 1.99) * mm});
            skPoint(sketch, "E108", {"position": v(-12.19, 2.99) * mm});
            skLineSegment(sketch, "E109", {"start": v(-11.59, 4.29) * mm, "end": v(-11.59, 1.69) * mm});
            skLineSegment(sketch, "E110", {"start": v(-12.19, 3.79) * mm, "end": v(-11.59, 4.29) * mm});
            skLineSegment(sketch, "E111", {"start": v(-12.19, 2.19) * mm, "end": v(-11.59, 1.69) * mm});
            skPoint(sketch, "E112.end.orphan", {"position": v(-11.59, 2.99) * mm});
            skLineSegment(sketch, "E113.trimOffspring", {"start": v(-12.19, 3.79) * mm, "end": v(-12.19, 4.99) * mm});
            skLineSegment(sketch, "E114.trimOffspring", {"start": v(-22.19, 3.99) * mm, "end": v(-22.19, 4.99) * mm});
            skPoint(sketch, "E115.end.orphan", {"position": v(-21.19, 2.99) * mm});
            skSolve(sketch);
        }
        {
            var Q0;
            Q0 = qSketchRegion(id + "F18", true);
            extrude(context, id + "F19", {"entities" : qUnion([Q0]), "oppositeDirection" : true, "depth" : 30 * mm});
        }
        {
            var Q0;
            Q0=makeQuery(id+"F19.opExtrude","SWEPT_EDGE",EDGE,{"disambiguationData":[OSD([sQuery(id+"F18.wireOp",EDGE,"E106"),sQuery(id+"F18.wireOp",EDGE,"E114.trimOffspring")])]});
            var Q1;
            Q1=makeQuery(id+"F19.opExtrude","SWEPT_EDGE",EDGE,{"disambiguationData":[OSD([sQuery(id+"F18.wireOp",EDGE,"E105"),sQuery(id+"F18.wireOp",EDGE,"E106")])]});
            var Q2;
            Q2=makeQuery(id+"F19.opExtrude","SWEPT_EDGE",EDGE,{"disambiguationData":[OSD([sQuery(id+"F18.wireOp",EDGE,"E105"),sQuery(id+"F18.wireOp",EDGE,"E107")])]});
            var Q3;
            Q3=makeQuery(id+"F19.opExtrude","SWEPT_EDGE",EDGE,{"disambiguationData":[OSD([sQuery(id+"F18.wireOp",EDGE,"E103.left"),sQuery(id+"F18.wireOp",EDGE,"E107")])]});
            fillet(context, id + "F20", {"entities" : qUnion([Q0, Q1, Q2, Q3]), "radius" : 0.2 * mm, "tangentPropagation" : true, "allowEdgeOverflow" : false});
        }
        {
            var Q0;
            Q0=makeQuery(id+"F19.opExtrude","SWEPT_EDGE",EDGE,{"disambiguationData":[OSD([sQuery(id+"F18.wireOp",EDGE,"E110"),sQuery(id+"F18.wireOp",EDGE,"E113.trimOffspring")])]});
            var Q1;
            Q1=makeQuery(id+"F19.opExtrude","SWEPT_EDGE",EDGE,{"disambiguationData":[OSD([sQuery(id+"F18.wireOp",EDGE,"E109"),sQuery(id+"F18.wireOp",EDGE,"E110")])]});
            var Q2;
            Q2=makeQuery(id+"F19.opExtrude","SWEPT_EDGE",EDGE,{"disambiguationData":[OSD([sQuery(id+"F18.wireOp",EDGE,"E109"),sQuery(id+"F18.wireOp",EDGE,"E111")])]});
            var Q3;
            Q3=makeQuery(id+"F19.opExtrude","SWEPT_EDGE",EDGE,{"disambiguationData":[OSD([sQuery(id+"F18.wireOp",EDGE,"E103.right"),sQuery(id+"F18.wireOp",EDGE,"E111")])]});
            fillet(context, id + "F21", {"entities" : qUnion([Q0, Q1, Q2, Q3]), "radius" : 0.16 * mm, "tangentPropagation" : true, "allowEdgeOverflow" : false});
        }
    });
